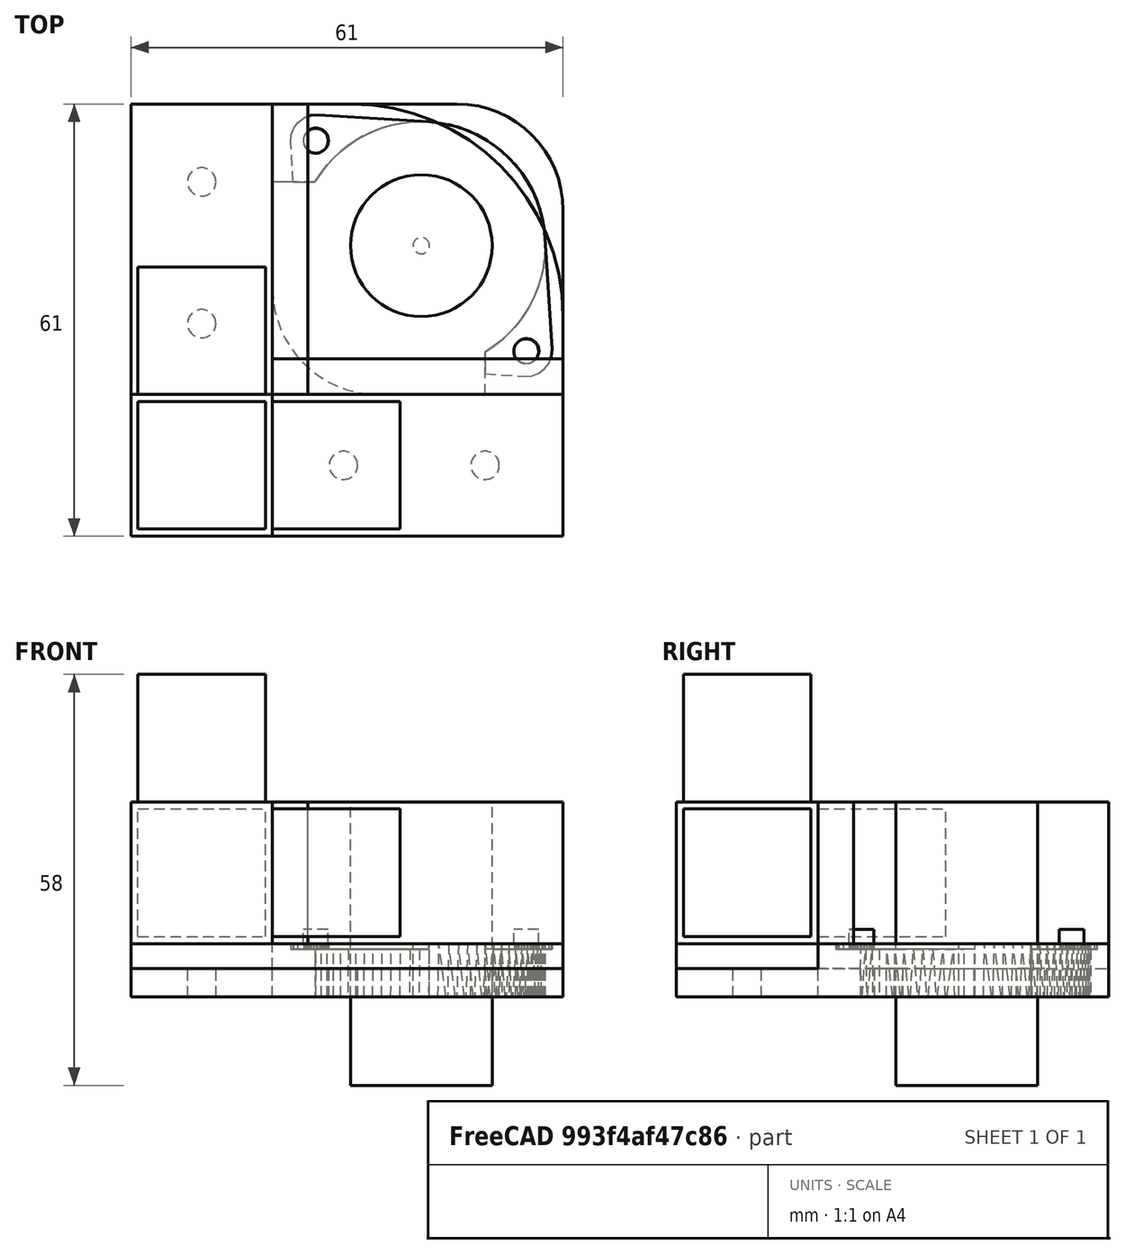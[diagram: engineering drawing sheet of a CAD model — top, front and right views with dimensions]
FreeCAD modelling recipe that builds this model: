
FCSTD DOCUMENT  (FreeCAD 0.19R24276 (Git))
Label: UnionXYZ
License: All rights reserved
LicenseURL: http://en.wikipedia.org/wiki/All_rights_reserved
objects: Part::Box×12, Part::Cut×10, Part::Cylinder×8, Part::Fuse×5, Part::Fillet×3, Mesh::Feature×1, Part::Feature×1
note: 39 computed .brp shape members not serialized (recipe doc carries the construction recipe); baked Part::Feature solids carry a one-line shape summary decoded from their .brp

FEATURE [Part::Box] Box  label="central"
  AttacherType = Attacher::AttachEngine3D
  Height = 20
  Length = 20
  Width = 20
FEATURE [Part::Box] Box001  label="X"
  AttacherType = Attacher::AttachEngine3D
  Height = 18
  Length = 18
  Placement = pos=(20,1,1) rot=(0,0,1;0rad)
  Width = 18
FEATURE [Part::Fuse] Fusion
  Base = -> Box
  Tool = -> Box001
FEATURE [Mesh::Feature] motor_Mitsumi_M35SP_11NK  label="motor_Mitsumi_M35SP-11NK"
  Placement = pos=(25,25,-1) rot=(0,0,1;-0.785398rad)
FEATURE [Part::Box] Box003  label="Z"
  AttacherType = Attacher::AttachEngine3D
  Height = 18
  Length = 18
  Placement = pos=(1,1,20) rot=(0,0,1;0rad)
  Width = 18
FEATURE [Part::Box] Box002  label="Y"
  AttacherType = Attacher::AttachEngine3D
  Height = 18
  Length = 18
  Placement = pos=(1,20,1) rot=(0,0,1;0rad)
  Width = 18
FEATURE [Part::Fuse] Fusion001
  Base = -> Fusion
  Tool = -> Box002
FEATURE [Part::Fuse] Fusion002  label="UnionXYZ"
  Base = -> Fusion001
  Tool = -> Box003
FEATURE [Part::Feature] motor_Mitsumi_M35SP_11NK001_solid  label="motor_Mitsumi_M35SP_11NK001 (Solid)"
  Placement = pos=(16,16,0.2) rot=(0,0,1;0rad)
  shape: bbox 36.88 x 36.88 x 16.9 mm, 3172 faces (baked)
FEATURE [Part::Box] Box005  label="Cube001"
  AttacherType = Attacher::AttachEngine3D
  Height = 7.5
  Length = 61
  Placement = pos=(0,0,-7.5) rot=(0,0,1;0rad)
  Width = 61
FEATURE [Part::Cut] Cut
  Base = -> Box005
  Tool = -> motor_Mitsumi_M35SP_11NK001_solid
FEATURE [Part::Fillet] Fillet
  Base = -> Cut
  Edges = 1 edges r=15: [Edge63]
FEATURE [Part::Cylinder] Cylinder
  Angle = 360
  AttacherType = Attacher::AttachEngine3D
  Height = 50
  Placement = pos=(10,50,-20) rot=(0,0,1;0rad)
  Radius = 2
FEATURE [Part::Cylinder] Cylinder001
  Angle = 360
  AttacherType = Attacher::AttachEngine3D
  Height = 50
  Placement = pos=(10,30,-20) rot=(0,0,1;0rad)
  Radius = 2
FEATURE [Part::Box] Box006  label="Cube"
  AttacherType = Attacher::AttachEngine3D
  Height = 20
  Length = 20
  Placement = pos=(0,0,-3.5) rot=(0,0,1;0rad)
  Width = 70
FEATURE [Part::Box] Box007  label="Cube002"
  AttacherType = Attacher::AttachEngine3D
  Height = 20
  Length = 70
  Placement = pos=(0,0,-3.5) rot=(0,0,1;0rad)
  Width = 20
FEATURE [Part::Cut] Cut001
  Base = -> Fillet
  Tool = -> Box006
FEATURE [Part::Cut] Cut002
  Base = -> Cut001
  Tool = -> Box007
FEATURE [Part::Cut] Cut003
  Base = -> Cut002
  Tool = -> Cylinder001
FEATURE [Part::Cut] Cut004
  Base = -> Cut003
  Tool = -> Cylinder
FEATURE [Part::Cylinder] Cylinder002
  Angle = 360
  AttacherType = Attacher::AttachEngine3D
  Height = 40
  Placement = pos=(30,10,-20) rot=(0,0,1;0rad)
  Radius = 2
FEATURE [Part::Cylinder] Cylinder003
  Angle = 360
  AttacherType = Attacher::AttachEngine3D
  Height = 40
  Placement = pos=(50,10,-20) rot=(0,0,1;0rad)
  Radius = 2
FEATURE [Part::Cut] Cut005
  Base = -> Cut004
  Tool = -> Cylinder002
FEATURE [Part::Cut] Cut006  label="cutConAgujeros"
  Base = -> Cut005
  Tool = -> Cylinder003
FEATURE [Part::Box] Box008  label="Cube003"
  AttacherType = Attacher::AttachEngine3D
  Height = 40
  Length = 30
  Placement = pos=(20,20,-15) rot=(0,0,1;0rad)
  Width = 30
FEATURE [Part::Fillet] Fillet001
  Base = -> Box008
  Edges = 1 edges r=15: [Edge1]
FEATURE [Part::Cut] Cut007
  Base = -> Cut006
  Tool = -> Fillet001
FEATURE [Part::Box] Box009  label="Cube004"
  AttacherType = Attacher::AttachEngine3D
  Height = 10
  Length = 20
  Placement = pos=(20,20,-3.5) rot=(0,0,1;0rad)
  Width = 20
FEATURE [Part::Cut] Cut008
  Base = -> Cut007
  Tool = -> Box009
FEATURE [Part::Cylinder] Cylinder004
  Angle = 360
  AttacherType = Attacher::AttachEngine3D
  Height = 2
  Placement = pos=(55.8,26.1,0) rot=(0,0,1;0rad)
  Radius = 1.75
FEATURE [Part::Cylinder] Cylinder005
  Angle = 360
  AttacherType = Attacher::AttachEngine3D
  Height = 2
  Placement = pos=(26.1,55.8,0) rot=(0,0,1;0rad)
  Radius = 1.75
FEATURE [Part::Fuse] Fusion003
  Base = -> Cut008
  Tool = -> Cylinder004
FEATURE [Part::Fuse] Fusion004  label="MotorCoreXY"
  Base = -> Cylinder005
  Tool = -> Fusion003
FEATURE [Part::Box] Box010  label="Cube005"
  AttacherType = Attacher::AttachEngine3D
  Height = 7.5
  Length = 61
  Placement = pos=(0,0,-7.5) rot=(0,0,1;0rad)
  Width = 61
FEATURE [Part::Box] Box011  label="Cube006"
  AttacherType = Attacher::AttachEngine3D
  Height = 20
  Length = 41
  Placement = pos=(20,20,0) rot=(0,0,1;0rad)
  Width = 5
FEATURE [Part::Cylinder] Cylinder006  label="EjeRodamientos"
  Angle = 360
  AttacherType = Attacher::AttachEngine3D
  Height = 40
  Placement = pos=(41,41,-20) rot=(0,0,1;0rad)
  Radius = 1.15
FEATURE [Part::Fillet] Fillet002
  Base = -> Box010
  Edges = 1 edges r=30: [Edge7]
FEATURE [Part::Cut] Cut009
  Base = -> Fillet002
  Tool = -> Cylinder006
FEATURE [Part::Box] Box012  label="Cube007"
  AttacherType = Attacher::AttachEngine3D
  Height = 20
  Length = 5
  Placement = pos=(20,20,0) rot=(0,0,1;0rad)
  Width = 41
FEATURE [Part::Cylinder] Cylinder007  label="EjeRodamientos001"
  Angle = 360
  AttacherType = Attacher::AttachEngine3D
  Height = 40
  Placement = pos=(41,41,-20) rot=(0,0,1;0rad)
  Radius = 10
